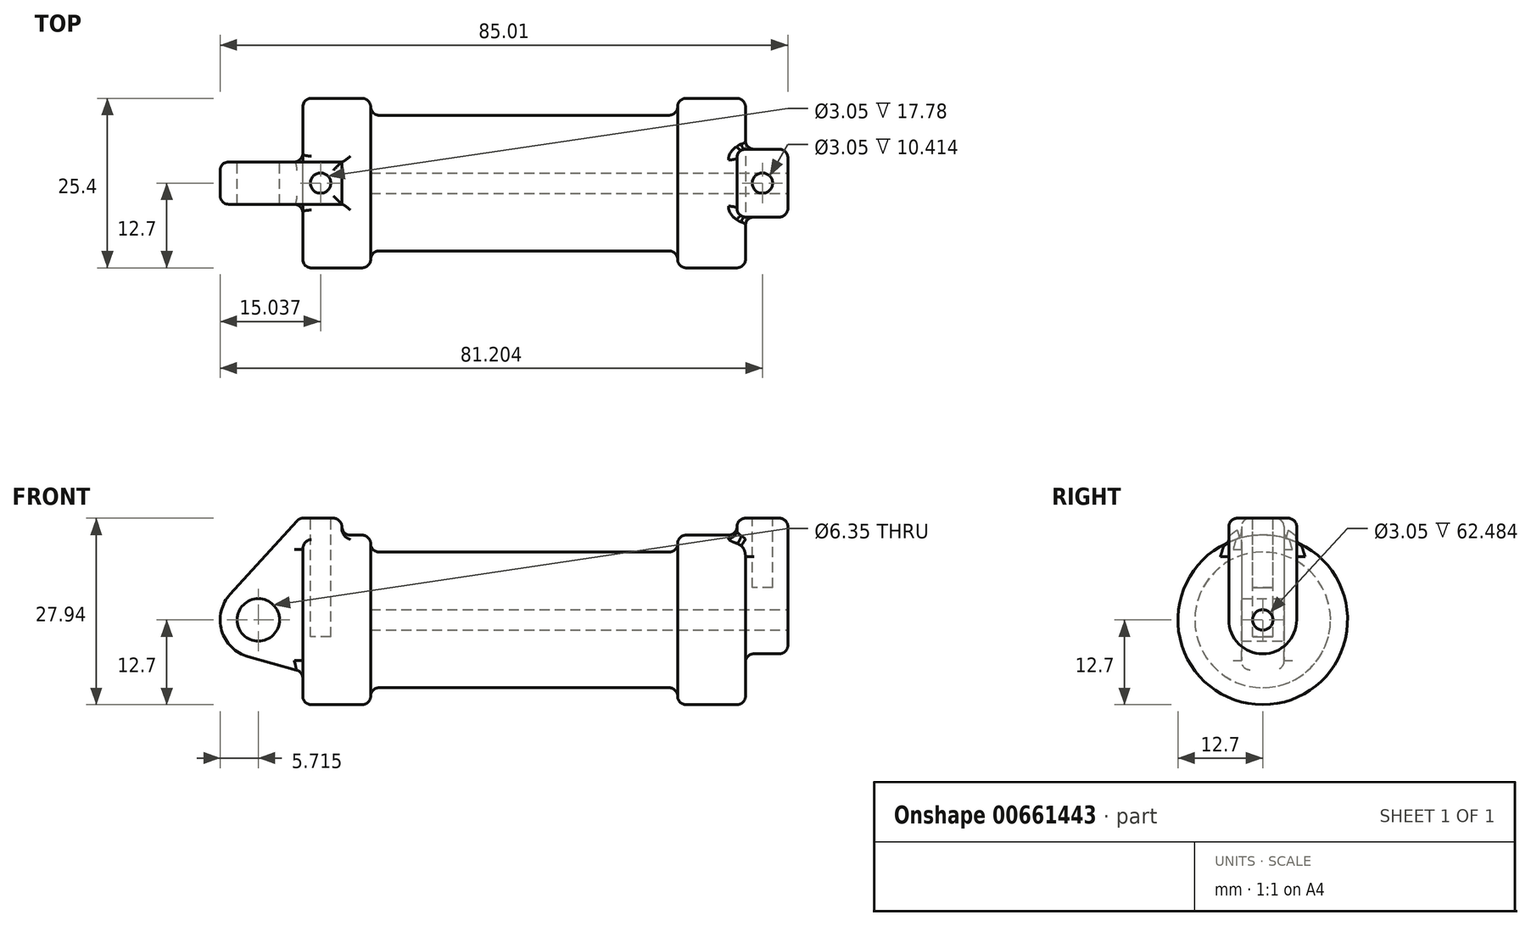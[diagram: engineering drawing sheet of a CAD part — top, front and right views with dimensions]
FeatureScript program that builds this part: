
annotation { "Feature Type Name" : "Feature", "Feature Type Description" : "" }
export const myFeature = defineFeature(function(context is Context, id is Id, definition is map)
    precondition{}
    {
        {
            var Q0;
            Q0=qCreatedBy(makeId("Front.planeOp"),FACE);
            var sketch = newSketch(context, id + "F0", { "sketchPlane" : qUnion([Q0])});
            skLineSegment(sketch, "E0", {"start": v(0, 0) * mm, "end": v(0, 12.7) * mm});
            skLineSegment(sketch, "E1", {"start": v(0, 12.7) * mm, "end": v(10.16, 12.7) * mm});
            skLineSegment(sketch, "E2", {"start": v(10.16, 12.7) * mm, "end": v(10.16, 10.16) * mm});
            skLineSegment(sketch, "E3", {"start": v(10.16, 10.16) * mm, "end": v(56.13, 10.16) * mm});
            skLineSegment(sketch, "E4", {"start": v(56.13, 10.16) * mm, "end": v(56.13, 12.7) * mm});
            skLineSegment(sketch, "E5", {"start": v(56.13, 12.7) * mm, "end": v(66.3, 12.7) * mm});
            skLineSegment(sketch, "E6", {"start": v(66.3, 12.7) * mm, "end": v(66.3, 0) * mm});
            skLineSegment(sketch, "E7", {"start": v(66.3, 0) * mm, "end": v(0, 0) * mm});
            skLineSegment(sketch, "E8", {"start": v(5.84, 15.24) * mm, "end": v(-0.5, 15.24) * mm});
            skLineSegment(sketch, "E9", {"start": v(-0.5, 15.24) * mm, "end": v(-10.88, 3.85) * mm});
            skLineSegment(sketch, "E10", {"start": v(0, 0) * mm, "end": v(-6.65, 0) * mm});
            skCircle(sketch, "E11", {"center": v(-6.65, 0) * mm, "radius": 5.72 * mm});
            skCircle(sketch, "E12", {"center": v(-6.65, 0) * mm, "radius": 3.18 * mm});
            skLineSegment(sketch, "E13", {"start": v(5.84, 15.24) * mm, "end": v(5.84, -9.4) * mm});
            skLineSegment(sketch, "E14", {"start": v(5.84, -9.4) * mm, "end": v(-8.18, -5.5) * mm});
            skSolve(sketch);
        }
        {
            var Q0;
            {var subQ0=sQuery(id+"F0.wireOp",EDGE,"E0");Q0=makeQuery(id+"F0.imprint","IMPRINT",FACE,{"disambiguationData":[TD([[makeQuery(id+"F0.imprint","IMPRINT",EDGE,{"derivedFrom":subQ0}),-1.0]])]});}
            var Q1;
            {var subQ0=sQuery(id+"F0.wireOp",EDGE,"E2");Q1=makeQuery(id+"F0.imprint","IMPRINT",FACE,{"disambiguationData":[TD([[makeQuery(id+"F0.imprint","IMPRINT",EDGE,{"derivedFrom":subQ0}),-1.0]])]});}
            var Q2;
            Q2=sQuery(id+"F0.wireOp",EDGE,"E7");
            revolve(context, id + "F1", {"entities" : qUnion([Q0, Q1]), "axis" : qUnion([Q2]), "revolveType" : RevolveType.FULL});
        }
        {
            var Q0;
            {var subQ0=sQuery(id+"F0.wireOp",EDGE,"E0");Q0=makeQuery(id+"F0.imprint","IMPRINT",FACE,{"disambiguationData":[TD([[makeQuery(id+"F0.imprint","IMPRINT",EDGE,{"derivedFrom":subQ0}),-1.0]])]});}
            var Q1;
            {var subQ1=sQuery(id+"F0.wireOp",EDGE,"E0");Q1=makeQuery(id+"F0.imprint","IMPRINT",FACE,{"disambiguationData":[TD([[makeQuery(id+"F0.imprint","IMPRINT",EDGE,{"derivedFrom":subQ1}),1.0]])]});}
            var Q2;
            {var subQ5=sQuery(id+"F0.wireOp",EDGE,"E12");Q2=makeQuery(id+"F0.imprint","IMPRINT",FACE,{"disambiguationData":[TD([[makeQuery(id+"F0.imprint","IMPRINT",EDGE,{"derivedFrom":subQ5}),-1.0]])]});}
            var Q3;
            {var subQ0=sQuery(id+"F0.wireOp",EDGE,"E14");Q3=makeQuery(id+"F0.imprint","IMPRINT",FACE,{"disambiguationData":[TD([[makeQuery(id+"F0.imprint","IMPRINT",EDGE,{"derivedFrom":subQ0}),-1.0]])]});}
            extrude(context, id + "F2", {"entities" : qUnion([Q0, Q1, Q2, Q3]), "operationType" : NewBodyOperationType.ADD, "depth" : 6.35 * mm, "offsetDistance" : 25.4 * mm, "symmetric" : true});
        }
        {
            var Q0;
            Q0=makeQuery(id+"F1.opRevolve","SWEPT_FACE",FACE,{"disambiguationData":[OSD([sQuery(id+"F0.wireOp",EDGE,"E6")])]});
            var sketch = newSketch(context, id + "F3", { "sketchPlane" : qUnion([Q0])});
            skPoint(sketch, "E15.0", {"position": v(0, 0) * mm});
            skCircle(sketch, "E15.1", {"center": v(0, 0) * mm, "radius": 12.7 * mm});
            skPoint(sketch, "E15.2", {"position": v(0, 15.24) * mm});
            skCircle(sketch, "E16", {"center": v(0, 0) * mm, "radius": 1.52 * mm});
            skCircle(sketch, "E17", {"center": v(0, 0) * mm, "radius": 5.08 * mm});
            skLineSegment(sketch, "E18", {"start": v(-5.08, 15.24) * mm, "end": v(5.08, 15.24) * mm});
            skLineSegment(sketch, "E19", {"start": v(5.08, 0) * mm, "end": v(5.08, 15.24) * mm});
            skLineSegment(sketch, "E20", {"start": v(-5.08, 0) * mm, "end": v(-5.08, 15.24) * mm});
            skSolve(sketch);
        }
        {
            var Q0;
            {var subQ5=sQuery(id+"F3.wireOp",EDGE,"E18");Q0=makeQuery(id+"F3.imprint","IMPRINT",FACE,{"disambiguationData":[TD([[makeQuery(id+"F3.imprint","IMPRINT",EDGE,{"derivedFrom":subQ5}),-1.0]])]});}
            var Q1;
            {var subQ0=sQuery(id+"F3.wireOp",EDGE,"E19");var subQ1=sQuery(id+"F3.wireOp",EDGE,"E15.1");var subQ2=makeQuery(id+"F3.imprint","INTERSECT",VERTEX,{"derivedFrom":[subQ1,subQ0]});Q1=makeQuery(id+"F3.imprint","IMPRINT",FACE,{"disambiguationData":[TD([[makeQuery(id+"F3.imprint","IMPRINT",EDGE,{"disambiguationData":[TD([[subQ2,-1.0]])],"derivedFrom":subQ1}),1.0]])]});}
            var Q2;
            Q2=makeQuery(id+"F3.imprint","IMPRINT",FACE,{"disambiguationData":[TD([[makeQuery(id+"F3.imprint","IMPRINT",EDGE,{"derivedFrom":sQuery(id+"F3.wireOp",EDGE,"E16")}),-1.0]])]});
            extrude(context, id + "F4", {"entities" : qUnion([Q0, Q1, Q2]), "operationType" : NewBodyOperationType.ADD, "oppositeDirection" : true, "depth" : 1.27 * mm, "offsetDistance" : 25.4 * mm, "hasSecondDirection" : true, "secondDirectionOppositeDirection" : false, "secondDirectionDepth" : 6.35 * mm});
        }
        {
            var Q0;
            Q0=makeQuery(id+"F3.imprint","IMPRINT",FACE,{"disambiguationData":[TD([[makeQuery(id+"F3.imprint","IMPRINT",EDGE,{"derivedFrom":sQuery(id+"F3.wireOp",EDGE,"E16")}),1.0]])]});
            var Q1;
            Q1=makeQuery(id+"F1.opRevolve","SWEPT_FACE",FACE,{"disambiguationData":[OSD([sQuery(id+"F0.wireOp",EDGE,"E2")])]});
            extrude(context, id + "F5", {"entities" : qUnion([Q0]), "operationType" : NewBodyOperationType.REMOVE, "endBound" : BoundingType.UP_TO_SURFACE, "oppositeDirection" : true, "depth" : 25.4 * mm, "endBoundEntityFace" : qUnion([Q1]), "offsetDistance" : 25.4 * mm});
        }
        {
            var Q0;
            Q0=makeQuery(id+"F2.opExtrude","SWEPT_FACE",FACE,{"disambiguationData":[OSD([sQuery(id+"F0.wireOp",EDGE,"E8")])]});
            var sketch = newSketch(context, id + "F6", { "sketchPlane" : qUnion([Q0])});
            skPoint(sketch, "E21.0", {"position": v(2.67, 3.18) * mm});
            skPoint(sketch, "E21.1", {"position": v(-0.5, 0) * mm});
            skPoint(sketch, "E21.2", {"position": v(2.67, -3.18) * mm});
            skPoint(sketch, "E21.3", {"position": v(5.84, 0) * mm});
            skCircle(sketch, "E22", {"center": v(2.67, 0) * mm, "radius": 1.52 * mm});
            skPoint(sketch, "E23.0", {"position": v(68.83, 5.08) * mm});
            skPoint(sketch, "E23.1", {"position": v(72.64, 0) * mm});
            skPoint(sketch, "E23.2", {"position": v(68.83, -5.08) * mm});
            skPoint(sketch, "E23.3", {"position": v(65.02, 0) * mm});
            skCircle(sketch, "E24", {"center": v(68.83, 0) * mm, "radius": 1.52 * mm});
            skSolve(sketch);
        }
        {
            var Q0;
            Q0=makeQuery(id+"F6.imprint","IMPRINT",FACE,{"disambiguationData":[TD([[makeQuery(id+"F6.imprint","IMPRINT",EDGE,{"derivedFrom":sQuery(id+"F6.wireOp",EDGE,"E22")}),1.0]])]});
            var Q1;
            Q1=sQuery(id+"F6.wireOp",EDGE,"E22");
            extrude(context, id + "F7", {"entities" : qUnion([Q0]), "operationType" : NewBodyOperationType.REMOVE, "surfaceEntities" : qUnion([Q1]), "oppositeDirection" : true, "depth" : 17.78 * mm, "offsetDistance" : 25.4 * mm});
        }
        {
            var Q0;
            Q0=makeQuery(id+"F6.imprint","IMPRINT",FACE,{"disambiguationData":[TD([[makeQuery(id+"F6.imprint","IMPRINT",EDGE,{"derivedFrom":sQuery(id+"F6.wireOp",EDGE,"E24")}),1.0]])]});
            extrude(context, id + "F8", {"entities" : qUnion([Q0]), "operationType" : NewBodyOperationType.REMOVE, "oppositeDirection" : true, "depth" : 10.4 * mm, "offsetDistance" : 25.4 * mm});
        }
        {
            var Q0;
            Q0=makeQuery(id+"F1.opRevolve","SWEPT_EDGE",EDGE,{"disambiguationData":[OSD([sQuery(id+"F0.wireOp",EDGE,"E2"),sQuery(id+"F0.wireOp",EDGE,"E3")])]});
            var Q1;
            Q1=makeQuery(id+"F1.opRevolve","SWEPT_EDGE",EDGE,{"disambiguationData":[OSD([sQuery(id+"F0.wireOp",EDGE,"E1"),sQuery(id+"F0.wireOp",EDGE,"E2")])]});
            var Q2;
            Q2=makeQuery(id+"F1.opRevolve","SWEPT_EDGE",EDGE,{"disambiguationData":[OSD([sQuery(id+"F0.wireOp",EDGE,"E0"),sQuery(id+"F0.wireOp",EDGE,"E1")])]});
            var Q3;
            Q3=makeQuery(id+"F1.opRevolve","SWEPT_EDGE",EDGE,{"disambiguationData":[OSD([sQuery(id+"F0.wireOp",EDGE,"E3"),sQuery(id+"F0.wireOp",EDGE,"E4")])]});
            var Q4;
            Q4=makeQuery(id+"F1.opRevolve","SWEPT_EDGE",EDGE,{"disambiguationData":[OSD([sQuery(id+"F0.wireOp",EDGE,"E4"),sQuery(id+"F0.wireOp",EDGE,"E5")])]});
            var Q5;
            Q5=makeQuery(id+"F1.opRevolve","SWEPT_EDGE",EDGE,{"disambiguationData":[OSD([sQuery(id+"F0.wireOp",EDGE,"E5"),sQuery(id+"F0.wireOp",EDGE,"E6")])]});
            fillet(context, id + "F9", {"entities" : qUnion([Q0, Q1, Q2, Q3, Q4, Q5]), "radius" : 1.27 * mm, "tangentPropagation" : true, "allowEdgeOverflow" : false});
        }
        {
            var Q0;
            Q0=makeQuery(id+"F2.boolean.opBoolean","INTERSECT",EDGE,{"derivedFrom":[makeQuery(id+"F1.opRevolve","SWEPT_FACE",FACE,{"disambiguationData":[OSD([sQuery(id+"F0.wireOp",EDGE,"E1")])]}),makeQuery(id+"F2.opExtrude","CAP_FACE",FACE,{"disambiguationData":[OSD([sQuery(id+"F0.wireOp",EDGE,"E8"),sQuery(id+"F0.wireOp",EDGE,"E9"),sQuery(id+"F0.wireOp",EDGE,"E11"),sQuery(id+"F0.wireOp",EDGE,"E12"),sQuery(id+"F0.wireOp",EDGE,"E13"),sQuery(id+"F0.wireOp",EDGE,"E14")])],"isStart":false})]});
            var Q1;
            Q1=makeQuery(id+"F2.boolean.opBoolean","INTERSECT",EDGE,{"derivedFrom":[makeQuery(id+"F1.opRevolve","SWEPT_FACE",FACE,{"disambiguationData":[OSD([sQuery(id+"F0.wireOp",EDGE,"E1")])]}),makeQuery(id+"F2.opExtrude","SWEPT_FACE",FACE,{"disambiguationData":[OSD([sQuery(id+"F0.wireOp",EDGE,"E13")])]})]});
            var Q2;
            Q2=makeQuery(id+"F2.boolean.opBoolean","INTERSECT",EDGE,{"derivedFrom":[makeQuery(id+"F1.opRevolve","SWEPT_FACE",FACE,{"disambiguationData":[OSD([sQuery(id+"F0.wireOp",EDGE,"E1")])]}),makeQuery(id+"F2.opExtrude","CAP_FACE",FACE,{"disambiguationData":[OSD([sQuery(id+"F0.wireOp",EDGE,"E8"),sQuery(id+"F0.wireOp",EDGE,"E9"),sQuery(id+"F0.wireOp",EDGE,"E11"),sQuery(id+"F0.wireOp",EDGE,"E12"),sQuery(id+"F0.wireOp",EDGE,"E13"),sQuery(id+"F0.wireOp",EDGE,"E14")])],"isStart":true})]});
            var Q3;
            Q3=makeQuery(id+"F2.boolean.opBoolean","INTERSECT",EDGE,{"derivedFrom":[makeQuery(id+"F1.opRevolve","SWEPT_FACE",FACE,{"disambiguationData":[OSD([sQuery(id+"F0.wireOp",EDGE,"E0")])]}),makeQuery(id+"F2.opExtrude","SWEPT_FACE",FACE,{"disambiguationData":[OSD([sQuery(id+"F0.wireOp",EDGE,"E14")])]})]});
            var Q4;
            Q4=makeQuery(id+"F2.opExtrude","CAP_EDGE",EDGE,{"disambiguationData":[OSD([sQuery(id+"F0.wireOp",EDGE,"E14")])],"isStart":true});
            var Q5;
            Q5=makeQuery(id+"F2.opExtrude","CAP_EDGE",EDGE,{"disambiguationData":[OSD([sQuery(id+"F0.wireOp",EDGE,"E11")])],"isStart":false});
            var Q6;
            Q6=makeQuery(id+"F2.opExtrude","CAP_EDGE",EDGE,{"disambiguationData":[OSD([sQuery(id+"F0.wireOp",EDGE,"E8")])],"isStart":true});
            var Q7;
            Q7=makeQuery(id+"F2.opExtrude","CAP_EDGE",EDGE,{"disambiguationData":[OSD([sQuery(id+"F0.wireOp",EDGE,"E8")])],"isStart":false});
            var Q8;
            Q8=makeQuery(id+"F2.opExtrude","SWEPT_EDGE",EDGE,{"disambiguationData":[OSD([sQuery(id+"F0.wireOp",EDGE,"E8"),sQuery(id+"F0.wireOp",EDGE,"E13")])]});
            var Q9;
            Q9=makeQuery(id+"F2.opExtrude","SWEPT_EDGE",EDGE,{"disambiguationData":[OSD([sQuery(id+"F0.wireOp",EDGE,"E8"),sQuery(id+"F0.wireOp",EDGE,"E9")])]});
            fillet(context, id + "F10", {"entities" : qUnion([Q0, Q1, Q2, Q3, Q4, Q5, Q6, Q7, Q8, Q9]), "radius" : 1.27 * mm, "tangentPropagation" : true, "allowEdgeOverflow" : false});
        }
        {
            var Q0;
            Q0=makeQuery(id+"F4.boolean.opBoolean","INTERSECT",EDGE,{"derivedFrom":[makeQuery(id+"F1.opRevolve","SWEPT_FACE",FACE,{"disambiguationData":[OSD([sQuery(id+"F0.wireOp",EDGE,"E5")])]}),makeQuery(id+"F4.opExtrude","CAP_FACE",FACE,{"disambiguationData":[OSD([sQuery(id+"F3.wireOp",EDGE,"E16"),sQuery(id+"F3.wireOp",EDGE,"E17"),sQuery(id+"F3.wireOp",EDGE,"E18"),sQuery(id+"F3.wireOp",EDGE,"E19"),sQuery(id+"F3.wireOp",EDGE,"E20")])],"isStart":false})]});
            var Q1;
            Q1=makeQuery(id+"F9.opFillet","BLEND_EDGE",EDGE,{"blendedFrom":[makeQuery(id+"F1.opRevolve","SWEPT_EDGE",EDGE,{"disambiguationData":[OSD([sQuery(id+"F0.wireOp",EDGE,"E5"),sQuery(id+"F0.wireOp",EDGE,"E6")])]}),makeQuery(id+"F4.opExtrude","SWEPT_FACE",FACE,{"disambiguationData":[OSD([sQuery(id+"F3.wireOp",EDGE,"E19")])]})],"blendedInto":[makeQuery(id+"F4.opExtrude","SWEPT_FACE",FACE,{"disambiguationData":[OSD([sQuery(id+"F3.wireOp",EDGE,"E19")])]})]});
            var Q2;
            Q2=makeQuery(id+"F4.opExtrude","CAP_EDGE",EDGE,{"disambiguationData":[OSD([sQuery(id+"F3.wireOp",EDGE,"E20")])],"isStart":true});
            var Q3;
            Q3=makeQuery(id+"F4.opExtrude","CAP_EDGE",EDGE,{"disambiguationData":[OSD([sQuery(id+"F3.wireOp",EDGE,"E18")])],"isStart":true});
            var Q4;
            Q4=makeQuery(id+"F4.opExtrude","SWEPT_EDGE",EDGE,{"disambiguationData":[OSD([sQuery(id+"F3.wireOp",EDGE,"E18"),sQuery(id+"F3.wireOp",EDGE,"E20")])]});
            var Q5;
            Q5=makeQuery(id+"F4.opExtrude","SWEPT_EDGE",EDGE,{"disambiguationData":[OSD([sQuery(id+"F3.wireOp",EDGE,"E18"),sQuery(id+"F3.wireOp",EDGE,"E19")])]});
            var Q6;
            Q6=makeQuery(id+"F4.opExtrude","CAP_EDGE",EDGE,{"disambiguationData":[OSD([sQuery(id+"F3.wireOp",EDGE,"E18")])],"isStart":false});
            var Q7;
            Q7=makeQuery(id+"F4.opExtrude","CAP_EDGE",EDGE,{"disambiguationData":[OSD([sQuery(id+"F3.wireOp",EDGE,"E19")])],"isStart":false});
            var Q8;
            Q8=makeQuery(id+"F4.opExtrude","CAP_EDGE",EDGE,{"disambiguationData":[OSD([sQuery(id+"F3.wireOp",EDGE,"E20")])],"isStart":false});
            fillet(context, id + "F11", {"entities" : qUnion([Q0, Q1, Q2, Q3, Q4, Q5, Q6, Q7, Q8]), "radius" : 1.27 * mm, "tangentPropagation" : true, "allowEdgeOverflow" : false});
        }
    });
